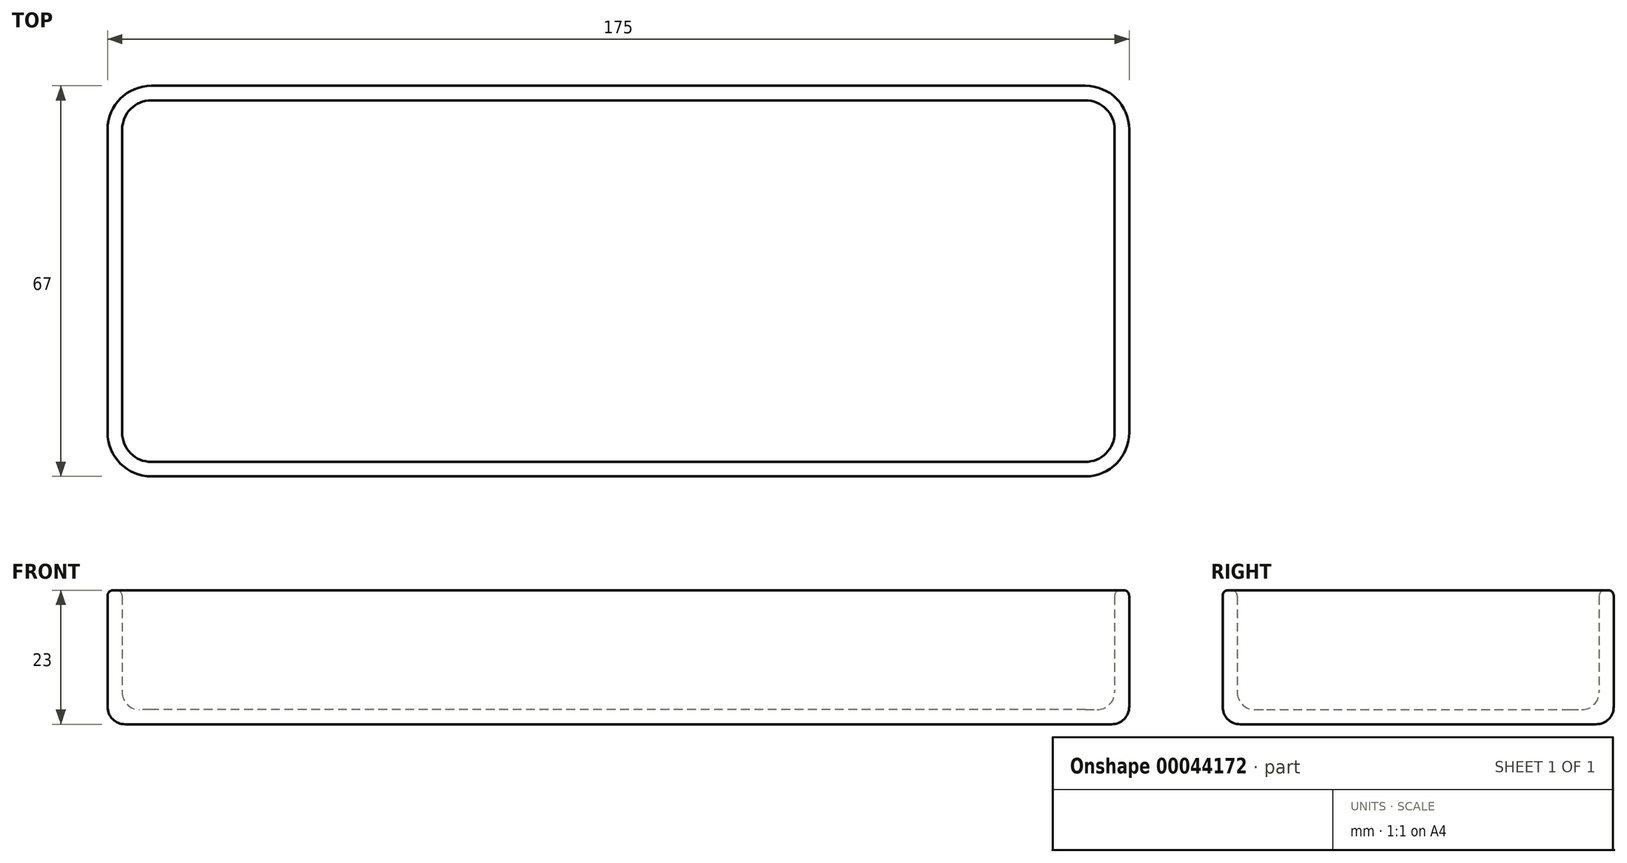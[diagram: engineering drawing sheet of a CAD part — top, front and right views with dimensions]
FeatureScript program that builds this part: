
annotation { "Feature Type Name" : "Feature", "Feature Type Description" : "" }
export const myFeature = defineFeature(function(context is Context, id is Id, definition is map)
    precondition{}
    {
        {
            var Q0;
            Q0=qCreatedBy(makeId("Top.planeOp"),FACE);
            var sketch = newSketch(context, id + "F0", { "sketchPlane" : qUnion([Q0])});
            skLineSegment(sketch, "E0.bottom", {"start": v(-79.23, 36.87) * mm, "end": v(80.77, 36.87) * mm});
            skLineSegment(sketch, "E0.top", {"start": v(-79.23, -25.13) * mm, "end": v(80.77, -25.13) * mm});
            skLineSegment(sketch, "E0.left", {"start": v(-84.23, 31.87) * mm, "end": v(-84.23, -20.13) * mm});
            skLineSegment(sketch, "E0.right", {"start": v(85.77, 31.87) * mm, "end": v(85.77, -20.13) * mm});
            skPoint(sketch, "E1.visualSharp", {"position": v(-84.23, 36.87) * mm});
            skArc(sketch, "E1.filletArc", {"start": v(-79.23, 36.87) * mm, "mid": v(-82.76, 35.4) * mm, "end": v(-84.23, 31.87) * mm});
            skPoint(sketch, "E2.visualSharp", {"position": v(85.77, 36.87) * mm});
            skArc(sketch, "E2.filletArc", {"start": v(85.77, 31.87) * mm, "mid": v(84.3, 35.4) * mm, "end": v(80.77, 36.87) * mm});
            skPoint(sketch, "E3.visualSharp", {"position": v(85.77, -25.13) * mm});
            skArc(sketch, "E3.filletArc", {"start": v(80.77, -25.13) * mm, "mid": v(84.3, -23.66) * mm, "end": v(85.77, -20.13) * mm});
            skPoint(sketch, "E4.visualSharp", {"position": v(-84.23, -25.13) * mm});
            skArc(sketch, "E4.filletArc", {"start": v(-84.23, -20.13) * mm, "mid": v(-82.76, -23.66) * mm, "end": v(-79.23, -25.13) * mm});
            skArc(sketch, "E5.0", {"start": v(-79.23, 39.37) * mm, "mid": v(-84.53, 37.17) * mm, "end": v(-86.73, 31.87) * mm});
            skLineSegment(sketch, "E5.1", {"start": v(-86.73, 31.87) * mm, "end": v(-86.73, -20.13) * mm});
            skLineSegment(sketch, "E5.2", {"start": v(-79.23, 39.37) * mm, "end": v(80.77, 39.37) * mm});
            skArc(sketch, "E5.3", {"start": v(-86.73, -20.13) * mm, "mid": v(-84.53, -25.43) * mm, "end": v(-79.23, -27.63) * mm});
            skArc(sketch, "E5.4", {"start": v(88.27, 31.87) * mm, "mid": v(86.07, 37.17) * mm, "end": v(80.77, 39.37) * mm});
            skLineSegment(sketch, "E5.5", {"start": v(88.27, 31.87) * mm, "end": v(88.27, -20.13) * mm});
            skArc(sketch, "E5.6", {"start": v(80.77, -27.63) * mm, "mid": v(86.07, -25.43) * mm, "end": v(88.27, -20.13) * mm});
            skLineSegment(sketch, "E5.7", {"start": v(-79.23, -27.63) * mm, "end": v(80.77, -27.63) * mm});
            skSolve(sketch);
        }
        {
            var Q0;
            Q0 = qSketchRegion(id + "F0", true);
            var Q1;
            Q1=makeQuery(id+"F0.imprint","IMPRINT",FACE,{"disambiguationData":[TD([[makeQuery(id+"F0.imprint","IMPRINT",EDGE,{"derivedFrom":sQuery(id+"F0.wireOp",EDGE,"E0.bottom")}),-1.0]])]});
            extrude(context, id + "F1", {"entities" : qUnion([Q0, Q1]), "depth" : 2.5 * mm});
        }
        {
            var Q0;
            Q0 = qSketchRegion(id + "F0", true);
            extrude(context, id + "F2", {"entities" : qUnion([Q0]), "operationType" : NewBodyOperationType.ADD, "depth" : 23 * mm});
        }
        {
            var Q0;
            Q0=makeQuery(id+"F1.opExtrude","CAP_FACE",FACE,{"disambiguationData":[OSD([sQuery(id+"F0.wireOp",EDGE,"E5.0"),sQuery(id+"F0.wireOp",EDGE,"E5.1"),sQuery(id+"F0.wireOp",EDGE,"E5.2"),sQuery(id+"F0.wireOp",EDGE,"E5.3"),sQuery(id+"F0.wireOp",EDGE,"E5.4"),sQuery(id+"F0.wireOp",EDGE,"E5.5"),sQuery(id+"F0.wireOp",EDGE,"E5.6"),sQuery(id+"F0.wireOp",EDGE,"E5.7")])],"isStart":true});
            fillet(context, id + "F3", {"entities" : qUnion([Q0]), "radius" : 3 * mm, "tangentPropagation" : true, "allowEdgeOverflow" : false});
        }
        {
            var Q0;
            Q0=makeQuery(id+"F2.opExtrude","CAP_FACE",FACE,{"disambiguationData":[OSD([sQuery(id+"F0.wireOp",EDGE,"E0.bottom"),sQuery(id+"F0.wireOp",EDGE,"E0.top"),sQuery(id+"F0.wireOp",EDGE,"E0.left"),sQuery(id+"F0.wireOp",EDGE,"E0.right"),sQuery(id+"F0.wireOp",EDGE,"E1.filletArc"),sQuery(id+"F0.wireOp",EDGE,"E2.filletArc"),sQuery(id+"F0.wireOp",EDGE,"E3.filletArc"),sQuery(id+"F0.wireOp",EDGE,"E4.filletArc"),sQuery(id+"F0.wireOp",EDGE,"E5.0"),sQuery(id+"F0.wireOp",EDGE,"E5.1"),sQuery(id+"F0.wireOp",EDGE,"E5.2"),sQuery(id+"F0.wireOp",EDGE,"E5.3"),sQuery(id+"F0.wireOp",EDGE,"E5.4"),sQuery(id+"F0.wireOp",EDGE,"E5.5"),sQuery(id+"F0.wireOp",EDGE,"E5.6"),sQuery(id+"F0.wireOp",EDGE,"E5.7")])],"isStart":false});
            fillet(context, id + "F4", {"entities" : qUnion([Q0]), "radius" : 1 * mm, "tangentPropagation" : true, "allowEdgeOverflow" : false});
        }
        {
            var Q0;
            Q0=makeQuery(id+"F2.boolean.opBoolean","INTERSECT",EDGE,{"derivedFrom":[makeQuery(id+"F1.opExtrude","CAP_FACE",FACE,{"disambiguationData":[OSD([sQuery(id+"F0.wireOp",EDGE,"E5.0"),sQuery(id+"F0.wireOp",EDGE,"E5.1"),sQuery(id+"F0.wireOp",EDGE,"E5.2"),sQuery(id+"F0.wireOp",EDGE,"E5.3"),sQuery(id+"F0.wireOp",EDGE,"E5.4"),sQuery(id+"F0.wireOp",EDGE,"E5.5"),sQuery(id+"F0.wireOp",EDGE,"E5.6"),sQuery(id+"F0.wireOp",EDGE,"E5.7")])],"isStart":false}),makeQuery(id+"F2.opExtrude","SWEPT_FACE",FACE,{"disambiguationData":[OSD([sQuery(id+"F0.wireOp",EDGE,"E0.top")])]})]});
            var Q1;
            Q1=makeQuery(id+"F2.boolean.opBoolean","INTERSECT",EDGE,{"derivedFrom":[makeQuery(id+"F1.opExtrude","CAP_FACE",FACE,{"disambiguationData":[OSD([sQuery(id+"F0.wireOp",EDGE,"E5.0"),sQuery(id+"F0.wireOp",EDGE,"E5.1"),sQuery(id+"F0.wireOp",EDGE,"E5.2"),sQuery(id+"F0.wireOp",EDGE,"E5.3"),sQuery(id+"F0.wireOp",EDGE,"E5.4"),sQuery(id+"F0.wireOp",EDGE,"E5.5"),sQuery(id+"F0.wireOp",EDGE,"E5.6"),sQuery(id+"F0.wireOp",EDGE,"E5.7")])],"isStart":false}),makeQuery(id+"F2.opExtrude","SWEPT_FACE",FACE,{"disambiguationData":[OSD([sQuery(id+"F0.wireOp",EDGE,"E3.filletArc")])]})]});
            var Q2;
            Q2=makeQuery(id+"F2.boolean.opBoolean","INTERSECT",EDGE,{"derivedFrom":[makeQuery(id+"F1.opExtrude","CAP_FACE",FACE,{"disambiguationData":[OSD([sQuery(id+"F0.wireOp",EDGE,"E5.0"),sQuery(id+"F0.wireOp",EDGE,"E5.1"),sQuery(id+"F0.wireOp",EDGE,"E5.2"),sQuery(id+"F0.wireOp",EDGE,"E5.3"),sQuery(id+"F0.wireOp",EDGE,"E5.4"),sQuery(id+"F0.wireOp",EDGE,"E5.5"),sQuery(id+"F0.wireOp",EDGE,"E5.6"),sQuery(id+"F0.wireOp",EDGE,"E5.7")])],"isStart":false}),makeQuery(id+"F2.opExtrude","SWEPT_FACE",FACE,{"disambiguationData":[OSD([sQuery(id+"F0.wireOp",EDGE,"E0.bottom")])]})]});
            var Q3;
            Q3=makeQuery(id+"F2.boolean.opBoolean","INTERSECT",EDGE,{"derivedFrom":[makeQuery(id+"F1.opExtrude","CAP_FACE",FACE,{"disambiguationData":[OSD([sQuery(id+"F0.wireOp",EDGE,"E5.0"),sQuery(id+"F0.wireOp",EDGE,"E5.1"),sQuery(id+"F0.wireOp",EDGE,"E5.2"),sQuery(id+"F0.wireOp",EDGE,"E5.3"),sQuery(id+"F0.wireOp",EDGE,"E5.4"),sQuery(id+"F0.wireOp",EDGE,"E5.5"),sQuery(id+"F0.wireOp",EDGE,"E5.6"),sQuery(id+"F0.wireOp",EDGE,"E5.7")])],"isStart":false}),makeQuery(id+"F2.opExtrude","SWEPT_FACE",FACE,{"disambiguationData":[OSD([sQuery(id+"F0.wireOp",EDGE,"E2.filletArc")])]})]});
            var Q4;
            Q4=makeQuery(id+"F2.boolean.opBoolean","INTERSECT",EDGE,{"derivedFrom":[makeQuery(id+"F1.opExtrude","CAP_FACE",FACE,{"disambiguationData":[OSD([sQuery(id+"F0.wireOp",EDGE,"E5.0"),sQuery(id+"F0.wireOp",EDGE,"E5.1"),sQuery(id+"F0.wireOp",EDGE,"E5.2"),sQuery(id+"F0.wireOp",EDGE,"E5.3"),sQuery(id+"F0.wireOp",EDGE,"E5.4"),sQuery(id+"F0.wireOp",EDGE,"E5.5"),sQuery(id+"F0.wireOp",EDGE,"E5.6"),sQuery(id+"F0.wireOp",EDGE,"E5.7")])],"isStart":false}),makeQuery(id+"F2.opExtrude","SWEPT_FACE",FACE,{"disambiguationData":[OSD([sQuery(id+"F0.wireOp",EDGE,"E4.filletArc")])]})]});
            var Q5;
            Q5=makeQuery(id+"F2.boolean.opBoolean","INTERSECT",EDGE,{"derivedFrom":[makeQuery(id+"F1.opExtrude","CAP_FACE",FACE,{"disambiguationData":[OSD([sQuery(id+"F0.wireOp",EDGE,"E5.0"),sQuery(id+"F0.wireOp",EDGE,"E5.1"),sQuery(id+"F0.wireOp",EDGE,"E5.2"),sQuery(id+"F0.wireOp",EDGE,"E5.3"),sQuery(id+"F0.wireOp",EDGE,"E5.4"),sQuery(id+"F0.wireOp",EDGE,"E5.5"),sQuery(id+"F0.wireOp",EDGE,"E5.6"),sQuery(id+"F0.wireOp",EDGE,"E5.7")])],"isStart":false}),makeQuery(id+"F2.opExtrude","SWEPT_FACE",FACE,{"disambiguationData":[OSD([sQuery(id+"F0.wireOp",EDGE,"E0.left")])]})]});
            var Q6;
            Q6=makeQuery(id+"F2.boolean.opBoolean","INTERSECT",EDGE,{"derivedFrom":[makeQuery(id+"F1.opExtrude","CAP_FACE",FACE,{"disambiguationData":[OSD([sQuery(id+"F0.wireOp",EDGE,"E5.0"),sQuery(id+"F0.wireOp",EDGE,"E5.1"),sQuery(id+"F0.wireOp",EDGE,"E5.2"),sQuery(id+"F0.wireOp",EDGE,"E5.3"),sQuery(id+"F0.wireOp",EDGE,"E5.4"),sQuery(id+"F0.wireOp",EDGE,"E5.5"),sQuery(id+"F0.wireOp",EDGE,"E5.6"),sQuery(id+"F0.wireOp",EDGE,"E5.7")])],"isStart":false}),makeQuery(id+"F2.opExtrude","SWEPT_FACE",FACE,{"disambiguationData":[OSD([sQuery(id+"F0.wireOp",EDGE,"E1.filletArc")])]})]});
            var Q7;
            Q7=makeQuery(id+"F2.boolean.opBoolean","INTERSECT",EDGE,{"derivedFrom":[makeQuery(id+"F1.opExtrude","CAP_FACE",FACE,{"disambiguationData":[OSD([sQuery(id+"F0.wireOp",EDGE,"E5.0"),sQuery(id+"F0.wireOp",EDGE,"E5.1"),sQuery(id+"F0.wireOp",EDGE,"E5.2"),sQuery(id+"F0.wireOp",EDGE,"E5.3"),sQuery(id+"F0.wireOp",EDGE,"E5.4"),sQuery(id+"F0.wireOp",EDGE,"E5.5"),sQuery(id+"F0.wireOp",EDGE,"E5.6"),sQuery(id+"F0.wireOp",EDGE,"E5.7")])],"isStart":false}),makeQuery(id+"F2.opExtrude","SWEPT_FACE",FACE,{"disambiguationData":[OSD([sQuery(id+"F0.wireOp",EDGE,"E0.right")])]})]});
            fillet(context, id + "F5", {"entities" : qUnion([Q0, Q1, Q2, Q3, Q4, Q5, Q6, Q7]), "radius" : 3 * mm, "tangentPropagation" : true, "allowEdgeOverflow" : false});
        }
    });
